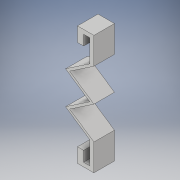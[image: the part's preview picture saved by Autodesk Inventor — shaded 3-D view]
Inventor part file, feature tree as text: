
AUTODESK INVENTOR PART (.ipt)
format: ipt  version: 2019 (Build 230136000, 136)  size: 124,416 bytes
history: native  units: in
note: dims shown in document units (in); Inventor stores cm internally (conversion verified against a paired STEP export)
features: extrude x1, sketch x1
ambient origin geometry x8: Origin, YZ Plane, XZ Plane, XY Plane, X Axis, Y Axis, Z Axis, Center Point
bodies: Solid1 (feature_tree)
feature tree (2):
  extrude  "Extrusion1"  Depth=0.0591in
  sketch  "Sketch1"  dims[d0=0.1378in d1=0.0591in d2=0.0984in d3=0.0591in d4=0.2165in d5=0.1575in d7=0.2559in d8=0.0in d9=0.3937in d10=0.315in d11=0.1575in d12=0.1969in d13=0.0in]
